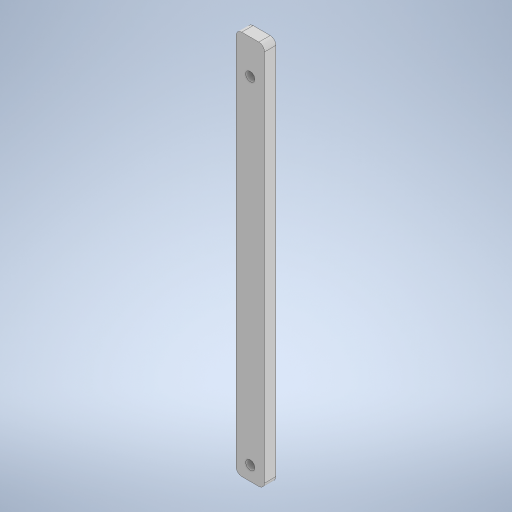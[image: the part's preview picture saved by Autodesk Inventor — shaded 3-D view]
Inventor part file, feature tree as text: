
AUTODESK INVENTOR PART (.ipt)
format: ipt  version: 2024.3 (Build 283343000, 343)  size: 252,928 bytes
history: native  units: mm
features: sketch x2, other x1, extrude x1, hole x1, fillet x1
ambient origin geometry x8: Origin, YZ Plane, XZ Plane, XY Plane, X Axis, Y Axis, Z Axis, Center Point
bodies: Body1 (feature_tree)
feature tree (6):
  other  "ソリッド1"
  extrude  "押し出し1"  Depth=10.0mm
  hole  "穴1"  [1 undecoded]
  fillet  "フィレット1"  Radius=4.0mm
  sketch  "スケッチ1"
  sketch  "スケッチ2"
note: 1 required parameter value undecoded (feature->parameter linkage not recoverable at this tier; creation-order binding heuristic only, values carry confidence <= 0.55)
